# Revit family: Electronics_Conferencing-Bars_Biamp_Parle_Audio_ABC-2500a_PMA 2000-DM
name_source: partatom
category: Communication Devices
units: mm (PartAtom-declared; Revit-internal decimal feet)

## family parameters
Cut with Voids When Loaded = No
Host = Face
Maintain Annotation Orientation = No
OmniClass Number = 23.85.10.11.14
OmniClass Title = Audio Equipment
Part Type = Normal
Room Calculation Point = No
Round Connector Dimension = Use Diameter
Shared = No

## types (2) — shared parameters
Altitude = 0-10,000 ft (0-3000m) MSL
Apparent Load = 60 VA
Audio Processing = AEC (Acoustic Echo Cancellation)
Bracket Material = Biamp - Metal - Black
Compliance = FCC Part 15B (USA) CE Marked (Europe) UL and C-UL listed (USA and Canada) RoHS Directive (Europe)
Connector Description = USB-C
Default Elevation = 3 mm  [stored 0.00984252 ft]
Depth = 64 mm
Description = Parlé™ ABC 2500 Conferencing Audio Bar
Height = 99 mm
Housing Material = Biamp - Plastic - Black
Humidity = 0-90% relative humidity (non-condensing)
Loudspeakers Frequency Response = -10 dB
Loudspeakers Sensitivity = 84 dB
Manufacturer = Biamp
Max Power Consumption = 60 W
Maximum SPL = 130 dB
Microphone Data Rate Output = 48 kHz
Microphone Frequency Response = -10dB
Microphone Indicators = Mute Indicator (Green/Red/Off LEDs)
Microphone Sensitivity = > -37dBFS ± 1dB
Microphone Technology = 27-Element Digital Array
Noise Reduction = AI filter
Nominal Beamwidth = 180° x 180°
Nominal Impedance = 4 ohm
Number of Poles = 1
Pickup Range = > 23 feet (7 m)
Polar Pattern = Active Beamformed
Power Factor = 1
Product Documentation Link = https://downloads.biamp.com
Product Page URL = https://www.biamp.com
Product data url = https://www.bimobject.com
Rated Maximum SPL = 90 dB (continuous)
SNR = 69 dB
Sampling Rate = 48 kHz
THD = < 0.2%
Temperature Range = 32 - 104° F (0 - 40° C)
Transducers = 2x 2.5 in (60 mm) full range
URL = https://www.biamp.com
USB 3.0 = 1x Type C
Version = 1
Voltage = 0 V
Weight = 9.60 lb
Width = 940 mm
connector = No

## per-type parameters (varying)
| type | Bottom | Config1 | Config2 | Top |
| Parle™ ABC 2500a Bottom mount | Yes | 3 | 2 | No |
| Parle™ ABC 2500a Top mount | No | 2 | 3 | Yes |

note: column(s) folded — value = type name in every type: Model

note: [stored X ft] marks values corroborated as IEEE doubles in the binary element streams (Revit-internal decimal feet)

## geometry (parser evidence)
native form markers: Sweep x18
no freeform markers — native parametric forms only
